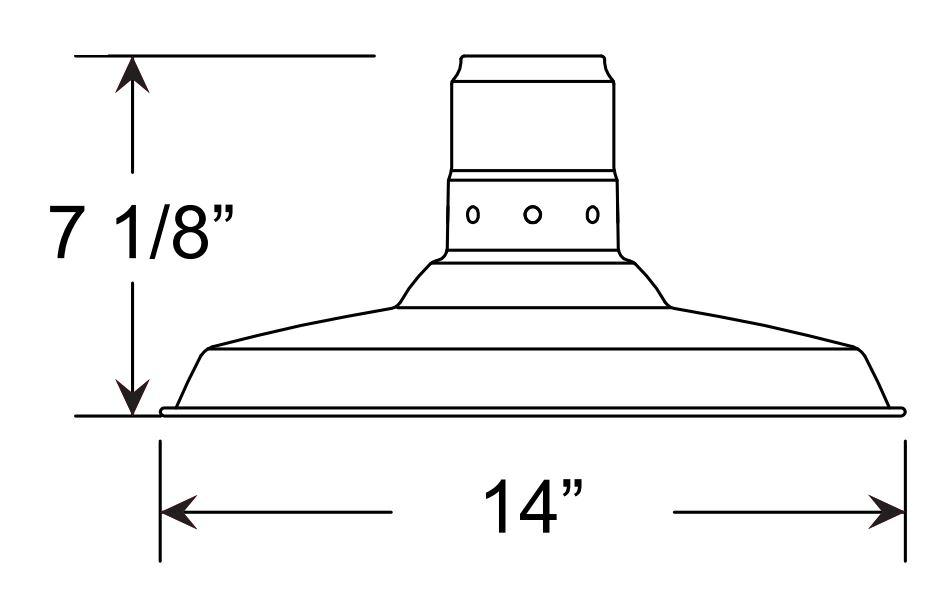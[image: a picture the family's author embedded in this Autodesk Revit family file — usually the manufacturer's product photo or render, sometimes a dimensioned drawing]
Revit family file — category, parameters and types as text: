
# Revit family: Vintage Bistro BEU
name_source: partatom
category: Lighting Fixtures
units: mm (PartAtom-declared; Revit-internal decimal feet)

## family parameters
Always vertical = Yes
Cut with Voids When Loaded = No
Light Source = Yes
OmniClass Number = 23.80.70.00
OmniClass Title = Lighting
Part Type = Normal
Room Calculation Point = No
Round Connector Dimension = Use Diameter
Shared = No
Work Plane-Based = No

## types (5) — shared parameters
Apparent Load = 200 VA
Body Colour = Spun aluminium
Body Material = Copper Clay
CRI = >90
Canopy Body = Copper Clay
Color Filter = 16777215
Construction Material = Heavy Duty spun aluminum.
Default Elevation = 0' - 0"
Description = 120-277 Voltage
Dimming = 1%
Dimming Lamp Color Temperature Shift = <None>
Efficiency = 65-125 lumens per watt
HUB = Putty
Lamp = MB
Life = L70 50,000 hours
Load Classification = Lighting
Manufacturer = ANP Lighting
Photometric Web File = generic
Power Factor = 1
Tilt Angle = 90.00°
URL = https://www.anplighting.com
Voltage = 120 V
Warranty = 5 year limited warranty
Wattage Comments = 200W
b = 0' - 3"

## per-type parameters (varying)
| type | BEU13 | BEU15 | BEU18 | BEU20 | BEU22 | Fixture Diameter | Fixture Height | Weight | a |
| BEU13 | Yes | No | No | No | No | 1' - 1" | 1' - 2 3/4" | 4.2 lb | 1' - 2" |
| BEU15 | No | Yes | No | No | No | 1' - 3" | 1' - 5" | 5.2 lb | 1' - 3" |
| BEU18 | No | No | Yes | No | No | 1' - 6" | 1' - 6 1/2" | 5.7 lbs | 1' - 2" |
| BEU20 | No | No | No | Yes | No | 1' - 8" | 1' - 8" | 6.7 lbs | 1' - 4" |
| BEU22 | No | No | No | No | Yes | 1' - 10" | 1' - 9" | 7.2 lbs | 1' - 6" |

note: column(s) folded — value = type name in every type: Model

## geometry (parser evidence)
native form markers: Sweep x38
no freeform markers — native parametric forms only
